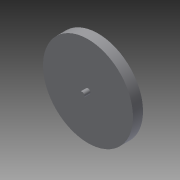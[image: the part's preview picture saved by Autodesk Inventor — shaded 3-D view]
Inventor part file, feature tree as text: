
AUTODESK INVENTOR PART (.ipt)
format: ipt  version: 2013 (Build 170138000, 138)  size: 91,648 bytes
history: native  units: mm
features: extrude x5, sketch x5, other x1
ambient origin geometry x8: Origin, YZ Plane, XZ Plane, XY Plane, X Axis, Y Axis, Z Axis, Center Point
feature tree (11):
  other  "ソリッド1"
  extrude  "押し出し1"  Depth=25.0mm
  extrude  "押し出し2"  Depth=5.0mm TaperAngle=0.0deg
  extrude  "押し出し3"  Depth=2.5mm
  extrude  "押し出し4"  Depth=3.0mm TaperAngle=0.0deg
  extrude  "押し出し5"  Depth=2.5mm
  sketch  "スケッチ1"
  sketch  "スケッチ2"
  sketch  "スケッチ3"
  sketch  "スケッチ4"
  sketch  "スケッチ5"
